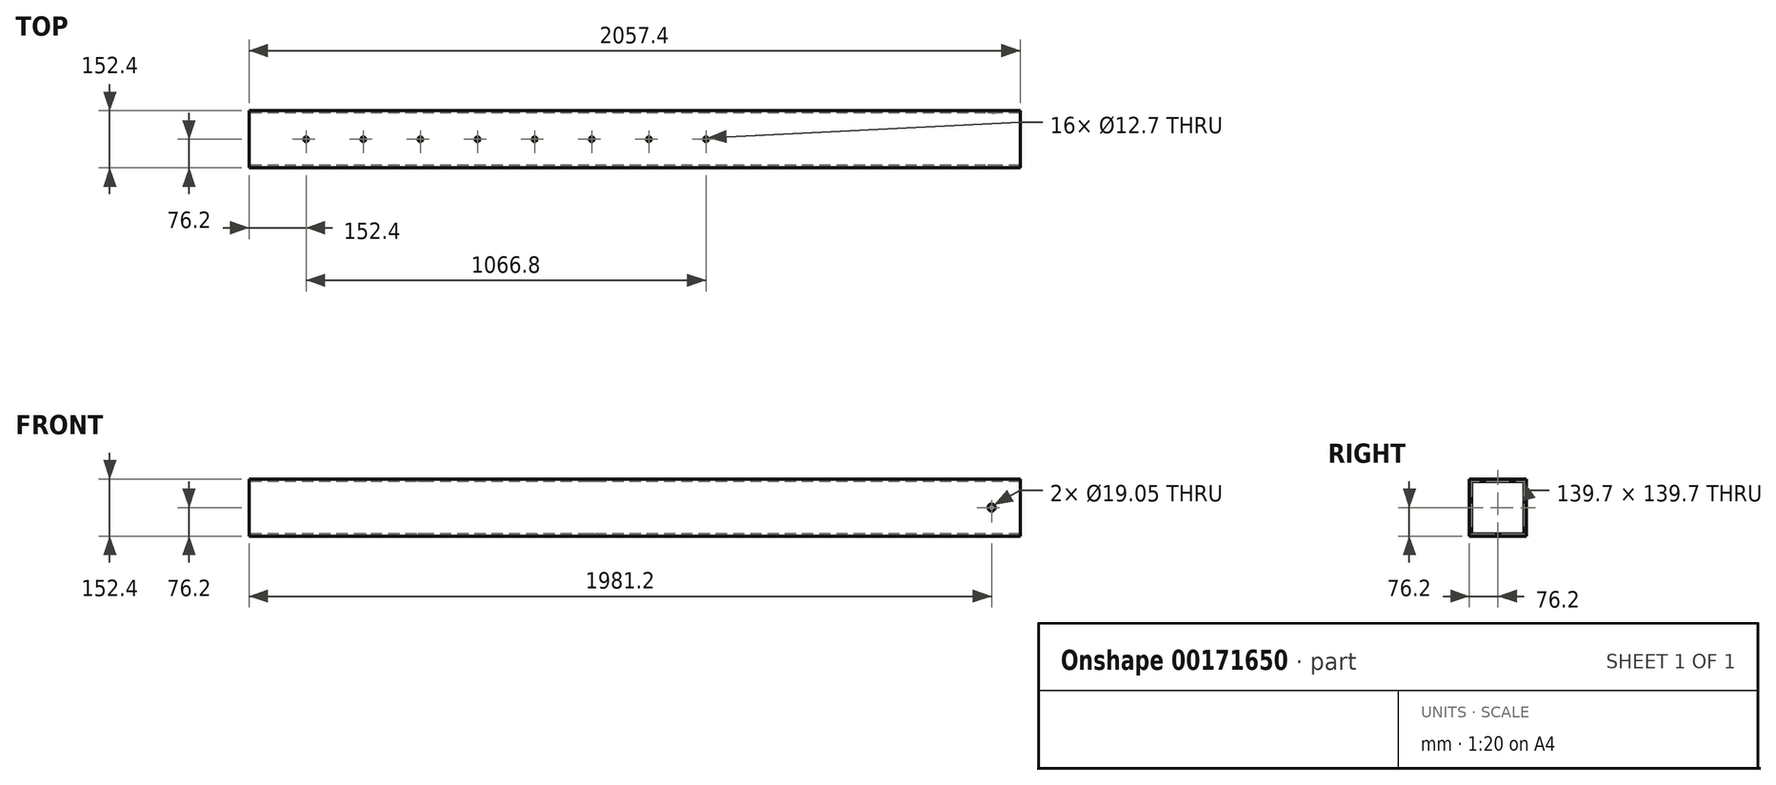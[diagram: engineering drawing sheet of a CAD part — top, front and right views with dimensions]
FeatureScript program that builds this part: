
annotation { "Feature Type Name" : "Feature", "Feature Type Description" : "" }
export const myFeature = defineFeature(function(context is Context, id is Id, definition is map)
    precondition{}
    {
        {
            var Q0;
            Q0=qCreatedBy(makeId("Right.planeOp"),FACE);
            var sketch = newSketch(context, id + "F0", { "sketchPlane" : qUnion([Q0])});
            skLineSegment(sketch, "E0.bottom", {"start": v(-76.2, 76.2) * mm, "end": v(76.2, 76.2) * mm});
            skLineSegment(sketch, "E0.top", {"start": v(-76.2, -76.2) * mm, "end": v(76.2, -76.2) * mm});
            skLineSegment(sketch, "E0.left", {"start": v(-76.2, 76.2) * mm, "end": v(-76.2, -76.2) * mm});
            skLineSegment(sketch, "E0.right", {"start": v(76.2, 76.2) * mm, "end": v(76.2, -76.2) * mm});
            skLineSegment(sketch, "E1.bottom", {"start": v(-69.85, 69.85) * mm, "end": v(69.85, 69.85) * mm});
            skLineSegment(sketch, "E1.top", {"start": v(-69.85, -69.85) * mm, "end": v(69.85, -69.85) * mm});
            skLineSegment(sketch, "E1.left", {"start": v(-69.85, 69.85) * mm, "end": v(-69.85, -69.85) * mm});
            skLineSegment(sketch, "E1.right", {"start": v(69.85, 69.85) * mm, "end": v(69.85, -69.85) * mm});
            skSolve(sketch);
        }
        {
            var Q0;
            Q0=makeQuery(id+"F0.imprint","IMPRINT",FACE,{"disambiguationData":[TD([[makeQuery(id+"F0.imprint","IMPRINT",EDGE,{"derivedFrom":sQuery(id+"F0.wireOp",EDGE,"E0.bottom")}),-1.0]])]});
            extrude(context, id + "F1", {"entities" : qUnion([Q0]), "depth" : 2057.4 * mm});
        }
        {
            var Q0;
            Q0=makeQuery(id+"F1.opExtrude","SWEPT_FACE",FACE,{"disambiguationData":[OSD([sQuery(id+"F0.wireOp",EDGE,"E0.bottom")])]});
            var sketch = newSketch(context, id + "F2", { "sketchPlane" : qUnion([Q0])});
            skPoint(sketch, "E2", {"position": v(152.4, 0) * mm});
            skPoint(sketch, "E3", {"position": v(304.8, 0) * mm});
            skPoint(sketch, "E4", {"position": v(457.2, 0) * mm});
            skPoint(sketch, "E5", {"position": v(609.6, 0) * mm});
            skPoint(sketch, "E6", {"position": v(762, 0) * mm});
            skPoint(sketch, "E7", {"position": v(914.4, 0) * mm});
            skPoint(sketch, "E8", {"position": v(1066.8, 0) * mm});
            skPoint(sketch, "E9", {"position": v(1219.2, 0) * mm});
            skSolve(sketch);
        }
        {
            var Q0;
            Q0=sQuery(id+"F2.wireOp",VERTEX,"E2");
            var Q1;
            Q1=sQuery(id+"F2.wireOp",VERTEX,"E3");
            var Q2;
            Q2=sQuery(id+"F2.wireOp",VERTEX,"E4");
            var Q3;
            Q3=sQuery(id+"F2.wireOp",VERTEX,"E5");
            var Q4;
            Q4=sQuery(id+"F2.wireOp",VERTEX,"E6");
            var Q5;
            Q5=sQuery(id+"F2.wireOp",VERTEX,"E7");
            var Q6;
            Q6=sQuery(id+"F2.wireOp",VERTEX,"E8");
            var Q7;
            Q7=sQuery(id+"F2.wireOp",VERTEX,"E9");
            var Q8;
            Q8=makeQuery(id+"F1.opExtrude","SWEPT_BODY",BODY,{"disambiguationData":[OSD([sQuery(id+"F0.wireOp",EDGE,"E0.bottom"),sQuery(id+"F0.wireOp",EDGE,"E0.top"),sQuery(id+"F0.wireOp",EDGE,"E0.left"),sQuery(id+"F0.wireOp",EDGE,"E0.right"),sQuery(id+"F0.wireOp",EDGE,"E1.bottom"),sQuery(id+"F0.wireOp",EDGE,"E1.top"),sQuery(id+"F0.wireOp",EDGE,"E1.left"),sQuery(id+"F0.wireOp",EDGE,"E1.right")])]});
            hole(context, id + "F3", {"style" : HoleStyle.SIMPLE, "endStyle" : HoleEndStyle.THROUGH, "holeDiameter" : 12.7 * mm, "locations" : qUnion([Q0, Q1, Q2, Q3, Q4, Q5, Q6, Q7]), "scope" : qUnion([Q8]), "isTappedThrough" : true});
        }
        {
            var Q0;
            Q0=makeQuery(id+"F1.opExtrude","SWEPT_FACE",FACE,{"disambiguationData":[OSD([sQuery(id+"F0.wireOp",EDGE,"E0.right")])]});
            var sketch = newSketch(context, id + "F4", { "sketchPlane" : qUnion([Q0])});
            skPoint(sketch, "E10", {"position": v(-1981.2, 0) * mm});
            skSolve(sketch);
        }
        {
            var Q0;
            Q0=sQuery(id+"F4.wireOp",VERTEX,"E10");
            var Q1;
            Q1=makeQuery(id+"F1.opExtrude","SWEPT_BODY",BODY,{"disambiguationData":[OSD([sQuery(id+"F0.wireOp",EDGE,"E0.bottom"),sQuery(id+"F0.wireOp",EDGE,"E0.top"),sQuery(id+"F0.wireOp",EDGE,"E0.left"),sQuery(id+"F0.wireOp",EDGE,"E0.right"),sQuery(id+"F0.wireOp",EDGE,"E1.bottom"),sQuery(id+"F0.wireOp",EDGE,"E1.top"),sQuery(id+"F0.wireOp",EDGE,"E1.left"),sQuery(id+"F0.wireOp",EDGE,"E1.right")])]});
            hole(context, id + "F5", {"style" : HoleStyle.SIMPLE, "endStyle" : HoleEndStyle.THROUGH, "holeDiameter" : 19.05 * mm, "locations" : qUnion([Q0]), "scope" : qUnion([Q1]), "isTappedThrough" : true});
        }
    });
